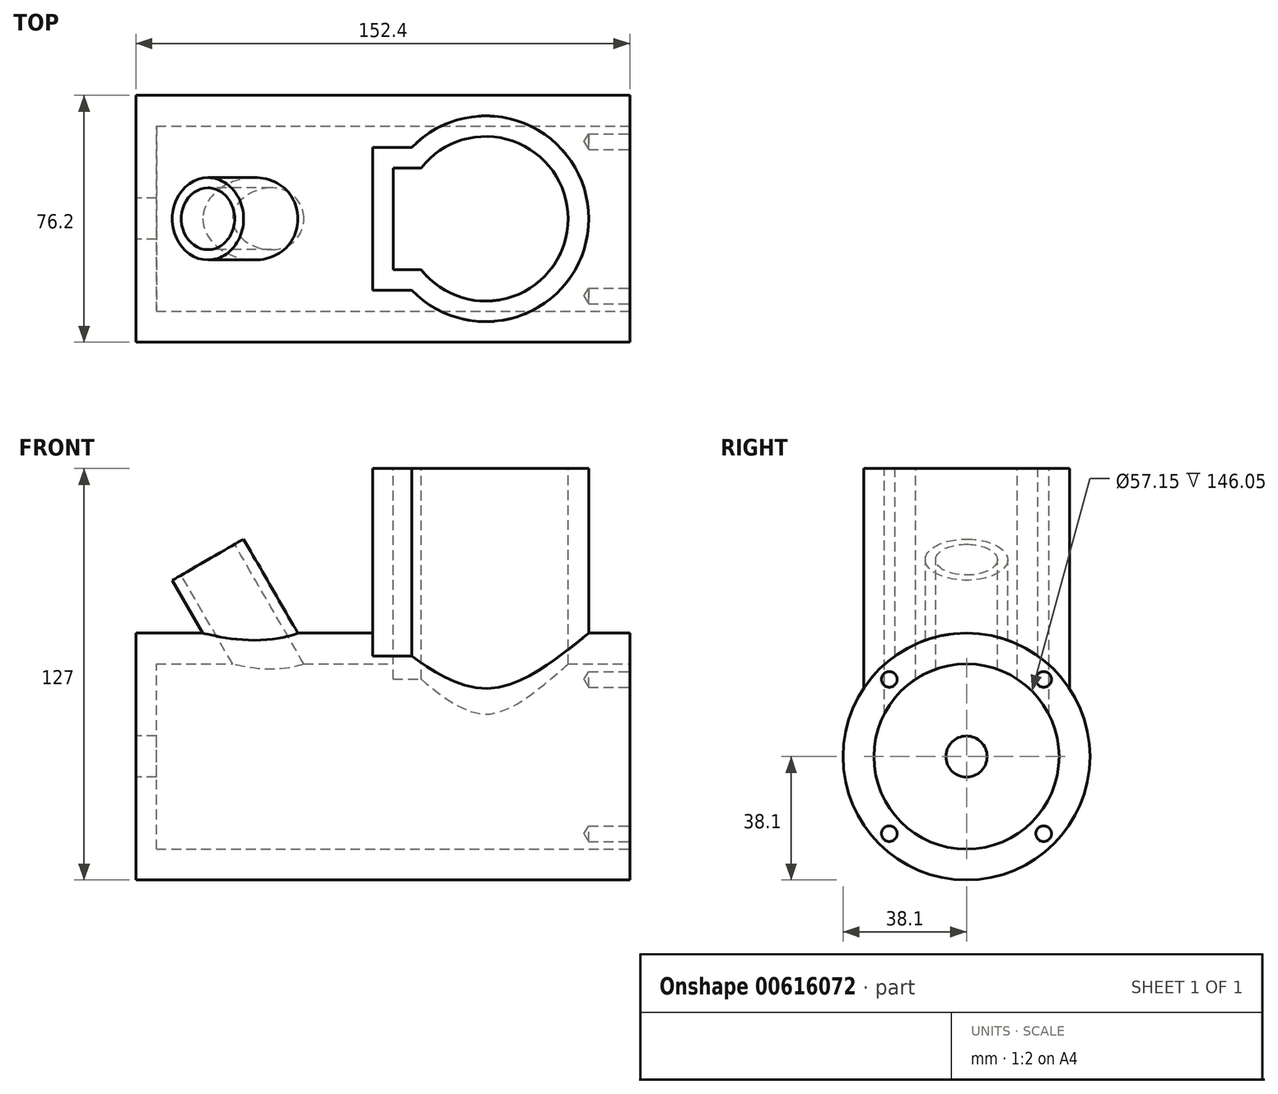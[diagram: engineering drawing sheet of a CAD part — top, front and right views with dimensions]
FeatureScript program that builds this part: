
annotation { "Feature Type Name" : "Feature", "Feature Type Description" : "" }
export const myFeature = defineFeature(function(context is Context, id is Id, definition is map)
    precondition{}
    {
        {
            var Q0;
            Q0=qCreatedBy(makeId("Front.planeOp"),FACE);
            var sketch = newSketch(context, id + "F0", { "sketchPlane" : qUnion([Q0])});
            skLineSegment(sketch, "E0", {"start": v(0, 0) * mm, "end": v(152.4, 0) * mm});
            skLineSegment(sketch, "E1", {"start": v(152.4, 0) * mm, "end": v(152.4, 38.1) * mm});
            skLineSegment(sketch, "E2", {"start": v(152.4, 38.1) * mm, "end": v(0, 38.1) * mm});
            skLineSegment(sketch, "E3", {"start": v(0, 38.1) * mm, "end": v(0, 0) * mm});
            skSolve(sketch);
        }
        {
            var Q0;
            Q0=makeQuery(id+"F0.imprint","IMPRINT",FACE,{"disambiguationData":[TD([[makeQuery(id+"F0.imprint","IMPRINT",EDGE,{"derivedFrom":sQuery(id+"F0.wireOp",EDGE,"E0")}),1.0]])]});
            var Q1;
            Q1=sQuery(id+"F0.wireOp",EDGE,"E0");
            revolve(context, id + "F1", {"entities" : qUnion([Q0]), "axis" : qUnion([Q1]), "revolveType" : RevolveType.FULL});
        }
        {
            var Q0;
            Q0=qCreatedBy(makeId("Top.planeOp"),FACE);
            cPlane(context, id + "F2", {"entities" : qUnion([Q0]), "cplaneType" : CPlaneType.OFFSET, "offset" : 38.1 * mm, "width" : 152.4 * mm, "height" : 152.4 * mm});
        }
        {
            var Q0;
            Q0=qCreatedBy(id+"F2.planeOp",FACE);
            var sketch = newSketch(context, id + "F3", { "sketchPlane" : qUnion([Q0])});
            skCircle(sketch, "E4", {"center": v(107.95, 0) * mm, "radius": 31.75 * mm});
            skSolve(sketch);
        }
        {
            var Q0;
            Q0=makeQuery(id+"F3.imprint","IMPRINT",FACE,{"disambiguationData":[TD([[makeQuery(id+"F3.imprint","IMPRINT",EDGE,{"derivedFrom":sQuery(id+"F3.wireOp",EDGE,"E4")}),1.0]])]});
            extrude(context, id + "F4", {"entities" : qUnion([Q0]), "operationType" : NewBodyOperationType.ADD, "oppositeDirection" : true, "depth" : 25.4 * mm, "offsetDistance" : 25.4 * mm});
        }
        {
            var Q0;
            Q0=makeQuery(id+"F4.opExtrude","CAP_FACE",FACE,{"disambiguationData":[OSD([sQuery(id+"F3.wireOp",EDGE,"E4")])],"isStart":true});
            extrude(context, id + "F5", {"entities" : qUnion([Q0]), "operationType" : NewBodyOperationType.ADD, "depth" : 50.8 * mm, "offsetDistance" : 25.4 * mm});
        }
        {
            var Q0;
            Q0=makeQuery(id+"F5.opExtrude","CAP_FACE",FACE,{"disambiguationData":[OSD([sQuery(id+"F3.wireOp",EDGE,"E4")])],"isStart":false});
            var sketch = newSketch(context, id + "F6", { "sketchPlane" : qUnion([Q0])});
            skLineSegment(sketch, "E5.bottom", {"start": v(85.1, -22.04) * mm, "end": v(73.03, -22.04) * mm});
            skLineSegment(sketch, "E5.top", {"start": v(85.1, 22.04) * mm, "end": v(73.03, 22.04) * mm});
            skLineSegment(sketch, "E5.left", {"start": v(85.1, -22.04) * mm, "end": v(85.1, 22.04) * mm});
            skLineSegment(sketch, "E5.right", {"start": v(73.03, -22.04) * mm, "end": v(73.03, 22.04) * mm});
            skPoint(sketch, "E6", {"position": v(107.95, 0) * mm});
            skSolve(sketch);
        }
        {
            var Q0;
            {var subQ0=sQuery(id+"F6.wireOp",EDGE,"E5.bottom");Q0=makeQuery(id+"F6.imprint","IMPRINT",FACE,{"disambiguationData":[TD([[makeQuery(id+"F6.imprint","IMPRINT",EDGE,{"derivedFrom":subQ0}),-1.0]])]});}
            extrude(context, id + "F7", {"entities" : qUnion([Q0]), "operationType" : NewBodyOperationType.ADD, "oppositeDirection" : true, "depth" : 76.2 * mm, "offsetDistance" : 25.4 * mm});
        }
        {
            var Q0;
            Q0=qCreatedBy(makeId("Front.planeOp"),FACE);
            var sketch = newSketch(context, id + "F8", { "sketchPlane" : qUnion([Q0])});
            skLineSegment(sketch, "E7", {"start": v(22.22, 60.77) * mm, "end": v(38.98, 31.75) * mm});
            skLineSegment(sketch, "E8", {"start": v(38.98, 31.75) * mm, "end": v(49.98, 38.1) * mm});
            skLineSegment(sketch, "E9", {"start": v(49.98, 38.1) * mm, "end": v(33.22, 67.12) * mm});
            skLineSegment(sketch, "E10", {"start": v(33.22, 67.12) * mm, "end": v(22.22, 60.77) * mm});
            skSolve(sketch);
        }
        {
            var Q0;
            Q0=makeQuery(id+"F8.imprint","IMPRINT",FACE,{"disambiguationData":[TD([[makeQuery(id+"F8.imprint","IMPRINT",EDGE,{"derivedFrom":sQuery(id+"F8.wireOp",EDGE,"E7")}),1.0]])]});
            var Q1;
            Q1=sQuery(id+"F8.wireOp",EDGE,"E7");
            revolve(context, id + "F9", {"operationType" : NewBodyOperationType.ADD, "entities" : qUnion([Q0]), "axis" : qUnion([Q1]), "revolveType" : RevolveType.FULL});
        }
        {
            var Q0;
            {var subQ0=sQuery(id+"F3.wireOp",EDGE,"E4");Q0=makeQuery(id+"F7.boolean.opBoolean","MERGE",FACE,{"derivedFrom":[makeQuery(id+"F5.opExtrude","CAP_FACE",FACE,{"disambiguationData":[OSD([subQ0])],"isStart":false}),makeQuery(id+"F7.opExtrude","CAP_FACE",FACE,{"disambiguationData":[OSD([subQ0,sQuery(id+"F6.wireOp",EDGE,"E5.bottom"),sQuery(id+"F6.wireOp",EDGE,"E5.top"),sQuery(id+"F6.wireOp",EDGE,"E5.right")])],"isStart":true})]});}
            var sketch = newSketch(context, id + "F10", { "sketchPlane" : qUnion([Q0])});
            skArc(sketch, "E11.0", {"start": v(87.98, -15.7) * mm, "mid": v(133.35, 0) * mm, "end": v(87.98, 15.7) * mm});
            skLineSegment(sketch, "E11.1", {"start": v(79.38, -15.7) * mm, "end": v(87.98, -15.7) * mm});
            skLineSegment(sketch, "E11.2", {"start": v(79.38, 15.7) * mm, "end": v(79.38, -15.7) * mm});
            skLineSegment(sketch, "E11.3", {"start": v(87.98, 15.7) * mm, "end": v(79.38, 15.7) * mm});
            skSolve(sketch);
        }
        {
            var Q0;
            Q0=makeQuery(id+"F10.imprint","IMPRINT",FACE,{"disambiguationData":[TD([[makeQuery(id+"F10.imprint","IMPRINT",EDGE,{"derivedFrom":sQuery(id+"F10.wireOp",EDGE,"E11.0")}),1.0]])]});
            extrude(context, id + "F11", {"entities" : qUnion([Q0]), "operationType" : NewBodyOperationType.REMOVE, "oppositeDirection" : true, "depth" : 76.2 * mm, "offsetDistance" : 25.4 * mm});
        }
        {
            var Q0;
            Q0=makeQuery(id+"F1.opRevolve","SWEPT_FACE",FACE,{"disambiguationData":[OSD([sQuery(id+"F0.wireOp",EDGE,"E1")])]});
            var sketch = newSketch(context, id + "F12", { "sketchPlane" : qUnion([Q0])});
            skCircle(sketch, "E12", {"center": v(0, 0) * mm, "radius": 28.57 * mm});
            skSolve(sketch);
        }
        {
            var Q0;
            Q0=makeQuery(id+"F12.imprint","IMPRINT",FACE,{"disambiguationData":[TD([[makeQuery(id+"F12.imprint","IMPRINT",EDGE,{"derivedFrom":sQuery(id+"F12.wireOp",EDGE,"E12")}),1.0]])]});
            var Q1;
            Q1 = qSketchRegion(id + "F14", true);
            extrude(context, id + "F13", {"entities" : qUnion([Q0, Q1]), "operationType" : NewBodyOperationType.REMOVE, "oppositeDirection" : true, "depth" : 146.05 * mm, "offsetDistance" : 25.4 * mm});
        }
        {
            var Q0;
            Q0=makeQuery(id+"F9.opRevolve","SWEPT_FACE",FACE,{"disambiguationData":[OSD([sQuery(id+"F8.wireOp",EDGE,"E10")])]});
            var sketch = newSketch(context, id + "F14", { "sketchPlane" : qUnion([Q0])});
            skCircle(sketch, "E13", {"center": v(49.63, 0) * mm, "radius": 9.52 * mm});
            skSolve(sketch);
        }
        {
            var Q0;
            Q0=makeQuery(id+"F14.imprint","IMPRINT",FACE,{"disambiguationData":[TD([[makeQuery(id+"F14.imprint","IMPRINT",EDGE,{"derivedFrom":sQuery(id+"F14.wireOp",EDGE,"E13")}),1.0]])]});
            extrude(context, id + "F15", {"entities" : qUnion([Q0]), "operationType" : NewBodyOperationType.REMOVE, "oppositeDirection" : true, "depth" : 50.8 * mm, "offsetDistance" : 25.4 * mm});
        }
        {
            var Q0;
            Q0=makeQuery(id+"F1.opRevolve","SWEPT_FACE",FACE,{"disambiguationData":[OSD([sQuery(id+"F0.wireOp",EDGE,"E1")])]});
            var sketch = newSketch(context, id + "F16", { "sketchPlane" : qUnion([Q0])});
            skPoint(sketch, "E14", {"position": v(-23.81, 23.81) * mm});
            skPoint(sketch, "E15", {"position": v(23.81, 23.81) * mm});
            skPoint(sketch, "E16", {"position": v(23.81, -23.81) * mm});
            skPoint(sketch, "E17", {"position": v(-23.81, -23.81) * mm});
            skSolve(sketch);
        }
        {
            var Q0;
            Q0=sQuery(id+"F16.wireOp",VERTEX,"E14");
            var Q1;
            Q1=sQuery(id+"F16.wireOp",VERTEX,"E15");
            var Q2;
            Q2=sQuery(id+"F16.wireOp",VERTEX,"E16");
            var Q3;
            Q3=sQuery(id+"F16.wireOp",VERTEX,"E17");
            var Q4;
            Q4=makeQuery(id+"F1.opRevolve","SWEPT_BODY",BODY,{"disambiguationData":[OSD([sQuery(id+"F0.wireOp",EDGE,"E0"),sQuery(id+"F0.wireOp",EDGE,"E1"),sQuery(id+"F0.wireOp",EDGE,"E2"),sQuery(id+"F0.wireOp",EDGE,"E3")])]});
            hole(context, id + "F17", {"style" : HoleStyle.SIMPLE, "endStyle" : HoleEndStyle.BLIND, "holeDiameter" : 4.83 * mm, "majorDiameter" : 6.35 * mm, "holeDepth" : 12.7 * mm, "isTappedThrough" : true, "tappedDepth" : 12.7 * mm, "tapClearance" : 3, "locations" : qUnion([Q0, Q1, Q2, Q3]), "scope" : qUnion([Q4])});
        }
        {
            var Q0;
            Q0=makeQuery(id+"F1.opRevolve","SWEPT_FACE",FACE,{"disambiguationData":[OSD([sQuery(id+"F0.wireOp",EDGE,"E3")])]});
            var sketch = newSketch(context, id + "F18", { "sketchPlane" : qUnion([Q0])});
            skPoint(sketch, "E18", {"position": v(0, 0) * mm});
            skSolve(sketch);
        }
        {
            var Q0;
            Q0=sQuery(id+"F18.wireOp",VERTEX,"E18");
            var Q1;
            Q1=makeQuery(id+"F1.opRevolve","SWEPT_BODY",BODY,{"disambiguationData":[OSD([sQuery(id+"F0.wireOp",EDGE,"E0"),sQuery(id+"F0.wireOp",EDGE,"E1"),sQuery(id+"F0.wireOp",EDGE,"E2"),sQuery(id+"F0.wireOp",EDGE,"E3")])]});
            hole(context, id + "F19", {"style" : HoleStyle.SIMPLE, "endStyle" : HoleEndStyle.BLIND, "holeDiameter" : 12.7 * mm, "majorDiameter" : 6.35 * mm, "holeDepth" : 12.7 * mm, "isTappedThrough" : true, "tappedDepth" : 12.7 * mm, "tapClearance" : 3, "locations" : qUnion([Q0]), "scope" : qUnion([Q1])});
        }
    });
